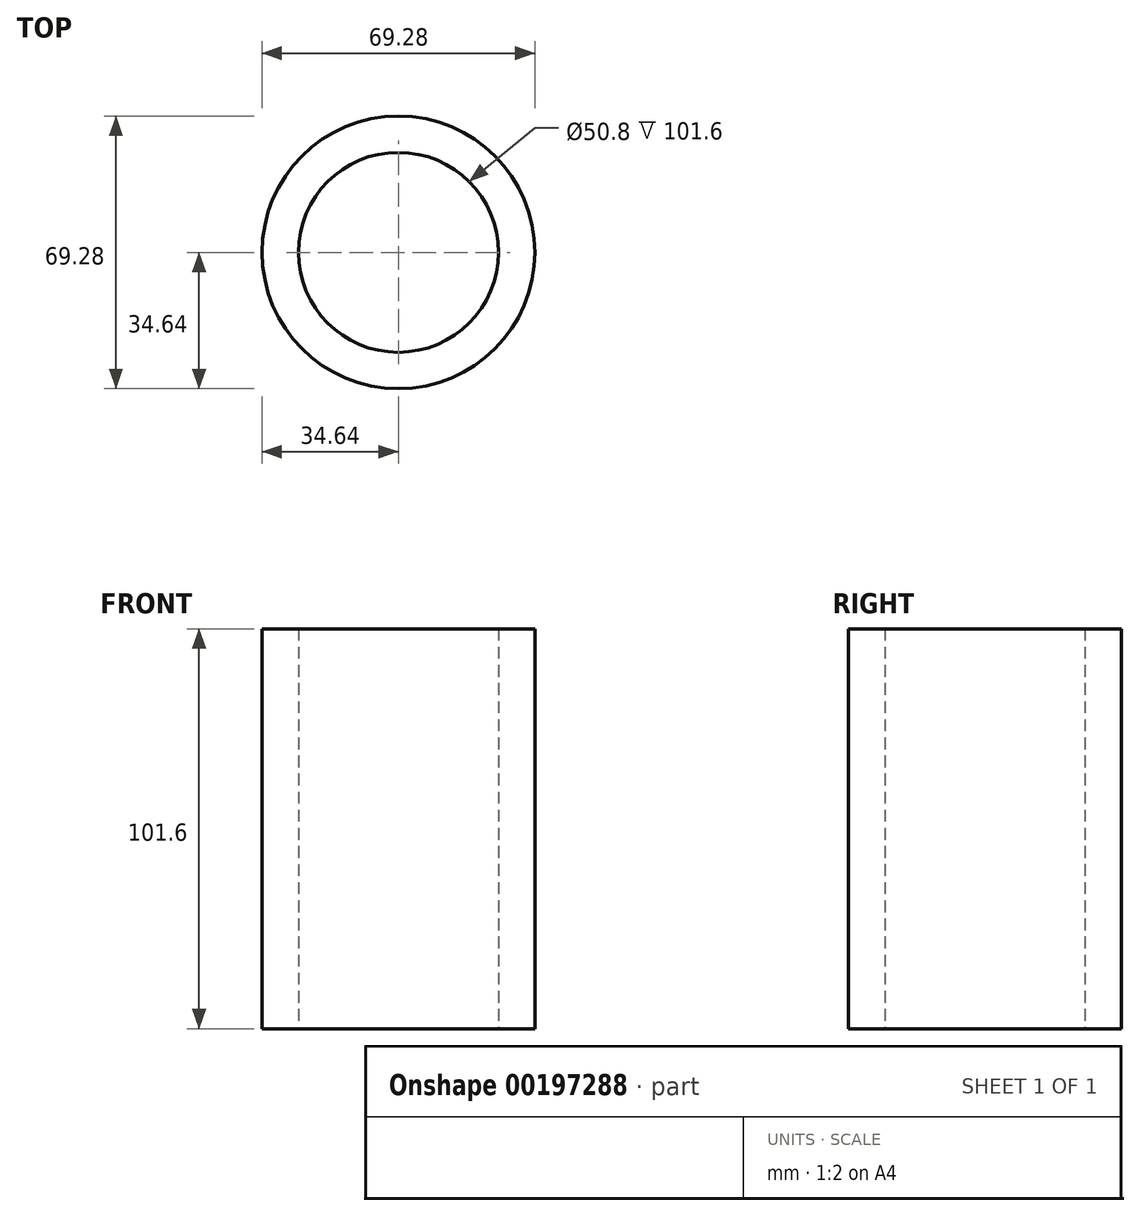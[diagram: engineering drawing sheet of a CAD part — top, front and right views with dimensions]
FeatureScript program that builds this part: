
annotation { "Feature Type Name" : "Feature", "Feature Type Description" : "" }
export const myFeature = defineFeature(function(context is Context, id is Id, definition is map)
    precondition{}
    {
        {
            var Q0;
            Q0=qCreatedBy(makeId("Top.planeOp"),FACE);
            var sketch = newSketch(context, id + "F0", { "sketchPlane" : qUnion([Q0])});
            skCircle(sketch, "E0", {"center": v(0, 0) * mm, "radius": 34.64 * mm});
            skSolve(sketch);
        }
        {
            var Q0;
            Q0 = qSketchRegion(id + "F0", true);
            extrude(context, id + "F1", {"entities" : qUnion([Q0]), "oppositeDirection" : true, "depth" : 101.6 * mm});
        }
        {
            var Q0;
            Q0=makeQuery(id+"F1.opExtrude","CAP_FACE",FACE,{"disambiguationData":[OSD([sQuery(id+"F0.wireOp",EDGE,"E0")])],"isStart":false});
            var sketch = newSketch(context, id + "F2", { "sketchPlane" : qUnion([Q0])});
            skCircle(sketch, "E1", {"center": v(0, 0) * mm, "radius": 25.4 * mm});
            skSolve(sketch);
        }
        {
            var Q0;
            Q0 = qSketchRegion(id + "F2", true);
            extrude(context, id + "F3", {"entities" : qUnion([Q0]), "operationType" : NewBodyOperationType.REMOVE, "endBound" : BoundingType.THROUGH_ALL, "oppositeDirection" : true, "depth" : 25.4 * mm});
        }
    });
